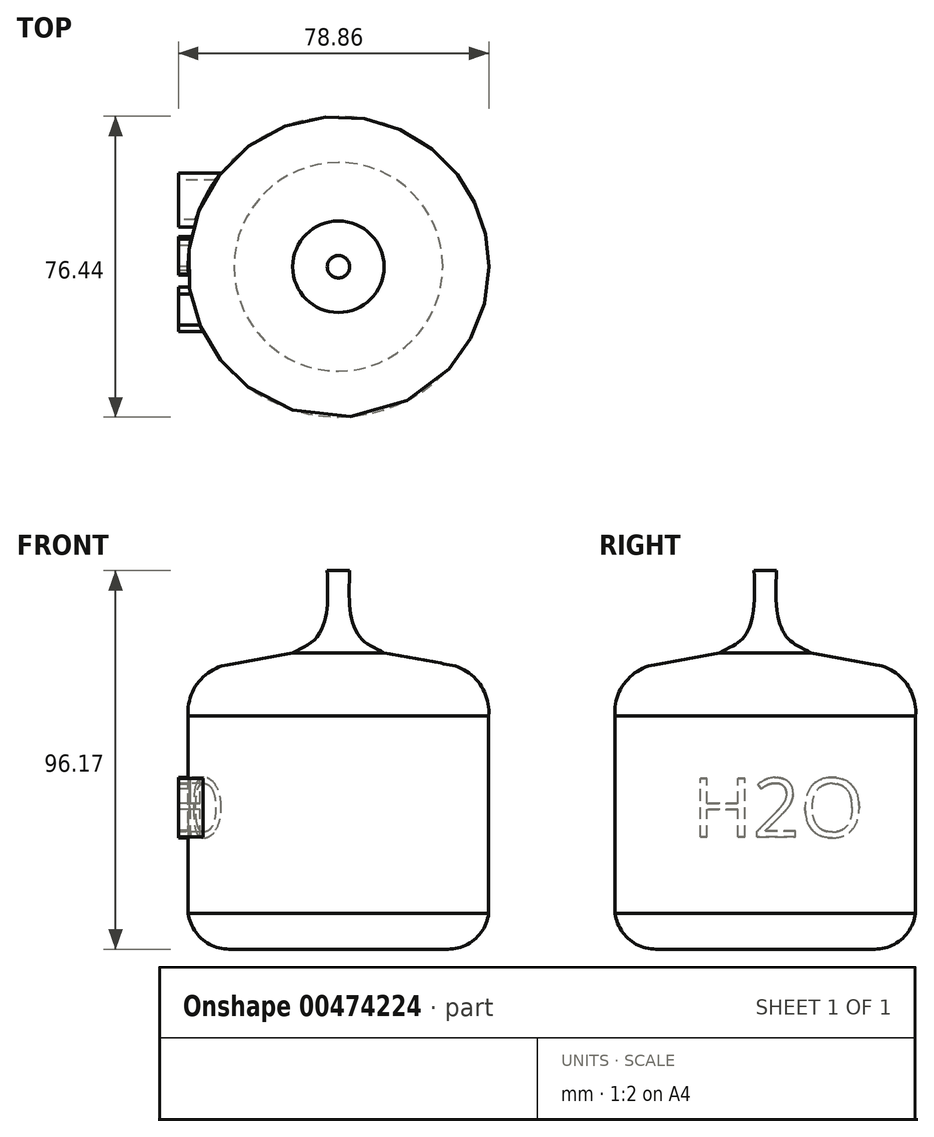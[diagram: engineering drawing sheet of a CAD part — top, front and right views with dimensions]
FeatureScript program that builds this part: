
annotation { "Feature Type Name" : "Feature", "Feature Type Description" : "" }
export const myFeature = defineFeature(function(context is Context, id is Id, definition is map)
    precondition{}
    {
        {
            var Q0;
            Q0=qCreatedBy(makeId("Front.planeOp"),FACE);
            var sketch = newSketch(context, id + "F0", { "sketchPlane" : qUnion([Q0])});
            skLineSegment(sketch, "E0", {"start": v(0, 0) * mm, "end": v(-26.5, 0) * mm});
            skArc(sketch, "E1", {"start": v(-26.5, 0) * mm, "mid": v(-34.18, 2.09) * mm, "end": v(-38.17, 8.97) * mm});
            skLineSegment(sketch, "E2", {"start": v(-38.17, 8.97) * mm, "end": v(-38.17, 59.15) * mm});
            skArc(sketch, "E3", {"start": v(-38.17, 59.15) * mm, "mid": v(-35.7, 67.62) * mm, "end": v(-28.17, 72.2) * mm});
            skLineSegment(sketch, "E4", {"start": v(-28.17, 72.2) * mm, "end": v(-11.62, 75.14) * mm});
            skFitSpline(sketch, "E5", {"points": [v(-11.62, 75.14) * mm, v(-6.06, 78.55) * mm, v(-3.1, 85.22) * mm, v(-2.85, 96.09) * mm], "startDerivative": vector(18.84, 12.12) * mm, "endDerivative": vector(-1.32, 29.75) * mm});
            skLineSegment(sketch, "E6", {"start": v(-2.85, 96.09) * mm, "end": v(0, 96.09) * mm});
            skLineSegment(sketch, "E7", {"start": v(0, 96.09) * mm, "end": v(0, 0) * mm});
            skSolve(sketch);
        }
        {
            var Q0;
            Q0=qCreatedBy(makeId("Front.planeOp"),FACE);
            var sketch = newSketch(context, id + "F1", { "sketchPlane" : qUnion([Q0])});
            skLineSegment(sketch, "E8", {"start": v(0, 106.34) * mm, "end": v(0, -16.43) * mm, "construction": true});
            skSolve(sketch);
        }
        {
            var Q0;
            Q0 = qSketchRegion(id + "F0", true);
            var Q1;
            Q1=sQuery(id+"F1.wireOp",EDGE,"E8");
            revolve(context, id + "F2", {"entities" : qUnion([Q0]), "axis" : qUnion([Q1]), "revolveType" : RevolveType.FULL});
        }
        {
            var Q0;
            Q0=qCreatedBy(makeId("Right.planeOp"),FACE);
            cPlane(context, id + "F3", {"entities" : qUnion([Q0]), "cplaneType" : CPlaneType.OFFSET, "offset" : 40.64 * mm, "oppositeDirection" : true, "width" : 152.4 * mm, "height" : 152.4 * mm});
        }
        {
            var Q0;
            Q0=qCreatedBy(id+"F3.planeOp",FACE);
            var sketch = newSketch(context, id + "F4", { "sketchPlane" : qUnion([Q0])});
            skText(sketch, "E9", { "text": "H2O\n", "fontName": "OpenSans-Regular.ttf"});
            const initialGuessF4  = {"E9": [-0.01855, 0.02839, 1, 0, 0.01506]};
            skSetInitialGuess(sketch, initialGuessF4);
            skSolve(sketch);
        }
        {
            var Q0;
            Q0 = qSketchRegion(id + "F4", true);
            extrude(context, id + "F5", {"entities" : qUnion([Q0]), "operationType" : NewBodyOperationType.ADD, "depth" : 25.4 * mm});
        }
    });
